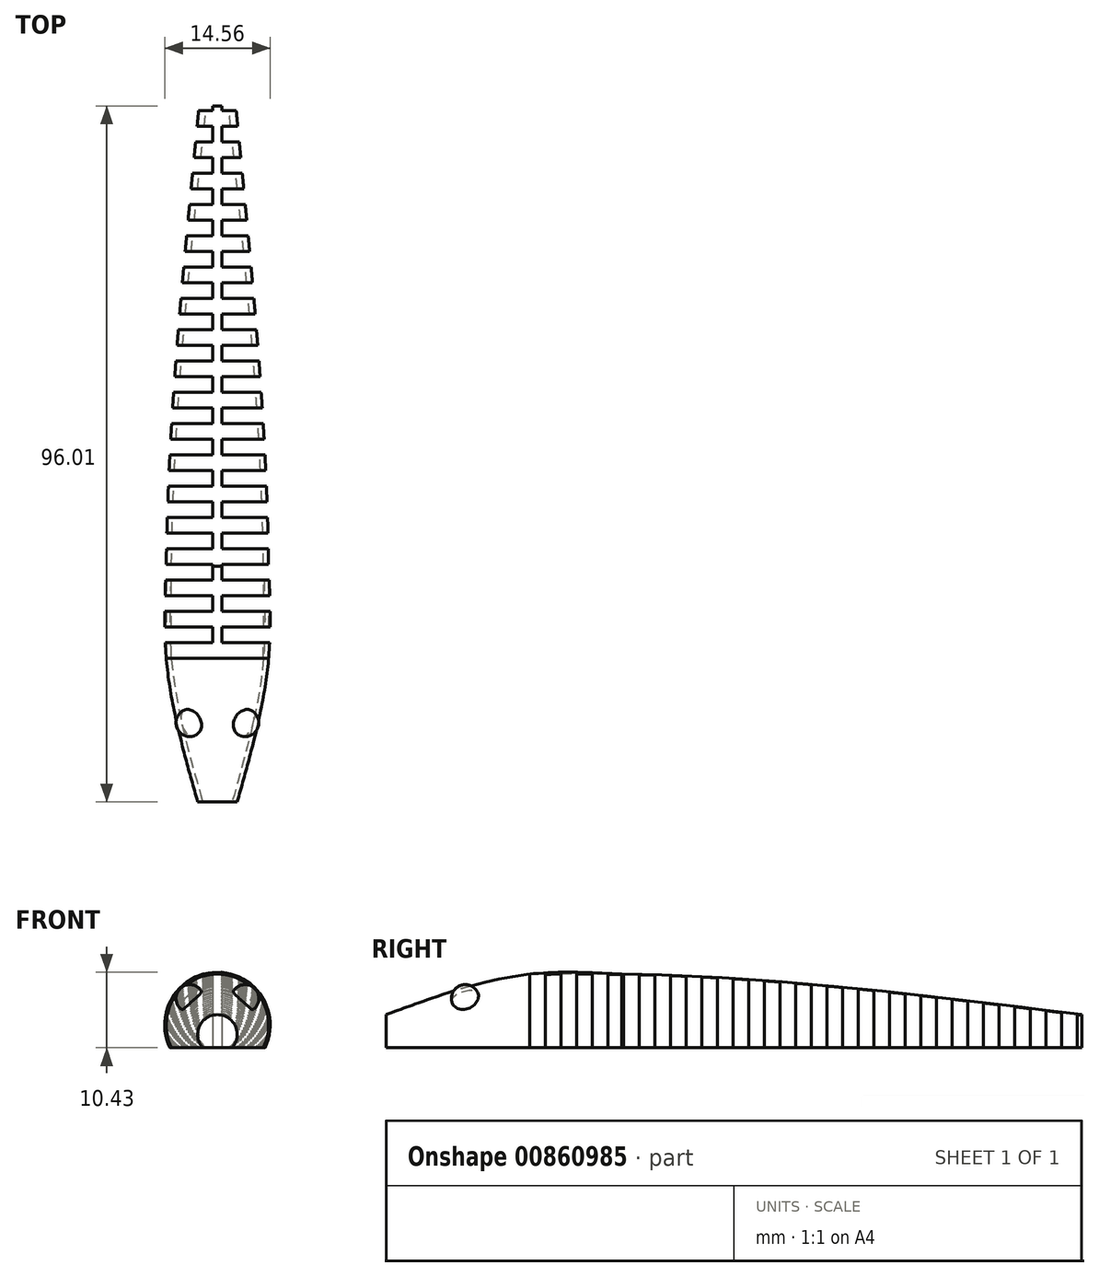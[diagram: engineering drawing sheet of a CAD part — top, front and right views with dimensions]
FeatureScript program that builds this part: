
annotation { "Feature Type Name" : "Feature", "Feature Type Description" : "" }
export const myFeature = defineFeature(function(context is Context, id is Id, definition is map)
    precondition{}
    {
        {
            var Q0;
            Q0=qCreatedBy(makeId("Front.planeOp"),FACE);
            var sketch = newSketch(context, id + "F0", { "sketchPlane" : qUnion([Q0])});
            skArc(sketch, "E0", {"start": v(6.35, 0) * mm, "mid": v(0, 10.16) * mm, "end": v(-6.35, 0) * mm});
            skPoint(sketch, "E0.first.point", {"position": v(-6.35, 0) * mm});
            skPoint(sketch, "E0.second.point", {"position": v(6.35, 0) * mm});
            skPoint(sketch, "E0.third.point", {"position": v(0, 10.16) * mm});
            skLineSegment(sketch, "E1", {"start": v(-6.35, 0) * mm, "end": v(6.35, 0) * mm});
            skSolve(sketch);
        }
        {
            var Q0;
            Q0=qCreatedBy(makeId("Front.planeOp"),FACE);
            cPlane(context, id + "F1", {"entities" : qUnion([Q0]), "cplaneType" : CPlaneType.OFFSET, "offset" : 12.7 * mm, "oppositeDirection" : true, "width" : 152.4 * mm, "height" : 152.4 * mm});
        }
        {
            var Q0;
            Q0=qCreatedBy(id+"F1.planeOp",FACE);
            var sketch = newSketch(context, id + "F2", { "sketchPlane" : qUnion([Q0])});
            skArc(sketch, "E2.0", {"start": v(6.35, 0) * mm, "mid": v(0, 10.16) * mm, "end": v(-6.35, 0) * mm});
            skLineSegment(sketch, "E2.1", {"start": v(-6.35, 0) * mm, "end": v(6.35, 0) * mm});
            skSolve(sketch);
        }
        {
            var Q0;
            Q0=qCreatedBy(id+"F1.planeOp",FACE);
            cPlane(context, id + "F3", {"entities" : qUnion([Q0]), "cplaneType" : CPlaneType.OFFSET, "offset" : 63.5 * mm, "oppositeDirection" : true, "width" : 152.4 * mm, "height" : 152.4 * mm});
        }
        {
            var Q0;
            Q0=qCreatedBy(id+"F3.planeOp",FACE);
            var sketch = newSketch(context, id + "F4", { "sketchPlane" : qUnion([Q0])});
            skPoint(sketch, "E3.0", {"position": v(0, 10.16) * mm});
            skPoint(sketch, "E4.0", {"position": v(6.35, 0) * mm});
            skPoint(sketch, "E5.0", {"position": v(-6.35, 0) * mm});
            skArc(sketch, "E6", {"start": v(1.52, 0) * mm, "mid": v(0, 4.57) * mm, "end": v(-1.52, 0) * mm});
            skPoint(sketch, "E6.first.point", {"position": v(1.52, 0) * mm});
            skPoint(sketch, "E6.second.point", {"position": v(-1.52, 0) * mm});
            skPoint(sketch, "E6.third.point", {"position": v(0, 4.57) * mm});
            skLineSegment(sketch, "E7", {"start": v(1.52, 0) * mm, "end": v(-1.52, 0) * mm});
            skSolve(sketch);
        }
        {
            var Q0;
            Q0=qCreatedBy(makeId("Front.planeOp"),FACE);
            cPlane(context, id + "F5", {"entities" : qUnion([Q0]), "cplaneType" : CPlaneType.OFFSET, "offset" : 19.8 * mm, "width" : 152.4 * mm, "height" : 152.4 * mm});
        }
        {
            var Q0;
            Q0=qCreatedBy(id+"F5.planeOp",FACE);
            var sketch = newSketch(context, id + "F6", { "sketchPlane" : qUnion([Q0])});
            skArc(sketch, "E8", {"start": v(2.03, 0) * mm, "mid": v(0, 4.57) * mm, "end": v(-2.03, 0) * mm});
            skPoint(sketch, "E8.first.point", {"position": v(-2.03, 0) * mm});
            skPoint(sketch, "E8.second.point", {"position": v(2.03, 0) * mm});
            skPoint(sketch, "E8.third.point", {"position": v(0, 4.57) * mm});
            skLineSegment(sketch, "E9", {"start": v(-2.03, 0) * mm, "end": v(2.03, 0) * mm});
            skSolve(sketch);
        }
        {
            var Q0;
            Q0=makeQuery(id+"F0.imprint","IMPRINT",FACE,{"disambiguationData":[TD([[makeQuery(id+"F0.imprint","IMPRINT",EDGE,{"derivedFrom":sQuery(id+"F0.wireOp",EDGE,"E0")}),1.0]])]});
            var Q1;
            Q1=makeQuery(id+"F2.imprint","IMPRINT",FACE,{"disambiguationData":[TD([[makeQuery(id+"F2.imprint","IMPRINT",EDGE,{"derivedFrom":sQuery(id+"F2.wireOp",EDGE,"E2.0")}),1.0]])]});
            var Q2;
            Q2=makeQuery(id+"F4.imprint","IMPRINT",FACE,{"disambiguationData":[TD([[makeQuery(id+"F4.imprint","IMPRINT",EDGE,{"derivedFrom":sQuery(id+"F4.wireOp",EDGE,"E6")}),1.0]])]});
            loft(context, id + "F7", {"sheetProfilesArray" : [{ "sheetProfileEntities" : qUnion([Q0]) }, { "sheetProfileEntities" : qUnion([Q1]) }, { "sheetProfileEntities" : qUnion([Q2]) }]});
        }
        {
            var Q0;
            Q0 = qSketchRegion(id + "F2", true);
            var Q1;
            Q1 = qSketchRegion(id + "F0", true);
            var Q2;
            Q2 = qSketchRegion(id + "F6", true);
            loft(context, id + "F8", {"sheetProfilesArray" : [{ "sheetProfileEntities" : qUnion([Q0]) }, { "sheetProfileEntities" : qUnion([Q1]) }, { "sheetProfileEntities" : qUnion([Q2]) }]});
        }
        {
            var Q0;
            Q0=qCreatedBy(makeId("Top.planeOp"),FACE);
            var sketch = newSketch(context, id + "F9", { "sketchPlane" : qUnion([Q0])});
            skLineSegment(sketch, "E10.bottom", {"start": v(-9.53, 2.16) * mm, "end": v(-0.64, 2.16) * mm});
            skLineSegment(sketch, "E10.top", {"start": v(-9.53, 4.32) * mm, "end": v(-0.64, 4.32) * mm});
            skLineSegment(sketch, "E10.left", {"start": v(-9.53, 2.16) * mm, "end": v(-9.53, 4.32) * mm});
            skLineSegment(sketch, "E10.right", {"start": v(-0.64, 2.16) * mm, "end": v(-0.64, 4.32) * mm});
            skLineSegment(sketch, "E11", {"start": v(0, -25.2) * mm, "end": v(0, 80.38) * mm, "construction": true});
            skLineSegment(sketch, "E12.0.1.0", {"start": v(-9.53, 6.48) * mm, "end": v(-9.53, 8.64) * mm});
            skLineSegment(sketch, "E12.0.1.1", {"start": v(-0.64, 6.48) * mm, "end": v(-0.64, 8.64) * mm});
            skLineSegment(sketch, "E12.0.1.2", {"start": v(-9.53, 8.64) * mm, "end": v(-0.64, 8.64) * mm});
            skLineSegment(sketch, "E12.0.1.3", {"start": v(-9.53, 6.48) * mm, "end": v(-0.64, 6.48) * mm});
            skLineSegment(sketch, "E12.0.2.0", {"start": v(-9.53, 10.8) * mm, "end": v(-9.53, 12.95) * mm});
            skLineSegment(sketch, "E12.0.2.1", {"start": v(-0.64, 10.8) * mm, "end": v(-0.64, 12.95) * mm});
            skLineSegment(sketch, "E12.0.2.2", {"start": v(-9.53, 12.95) * mm, "end": v(-0.64, 12.95) * mm});
            skLineSegment(sketch, "E12.0.2.3", {"start": v(-9.53, 10.8) * mm, "end": v(-0.64, 10.8) * mm});
            skLineSegment(sketch, "E12.0.3.0", {"start": v(-9.53, 15.11) * mm, "end": v(-9.53, 17.27) * mm});
            skLineSegment(sketch, "E12.0.3.1", {"start": v(-0.64, 15.11) * mm, "end": v(-0.64, 17.27) * mm});
            skLineSegment(sketch, "E12.0.3.2", {"start": v(-9.53, 17.27) * mm, "end": v(-0.64, 17.27) * mm});
            skLineSegment(sketch, "E12.0.3.3", {"start": v(-9.53, 15.11) * mm, "end": v(-0.64, 15.11) * mm});
            skLineSegment(sketch, "E12.0.4.0", {"start": v(-9.53, 19.43) * mm, "end": v(-9.53, 21.6) * mm});
            skLineSegment(sketch, "E12.0.4.1", {"start": v(-0.64, 19.43) * mm, "end": v(-0.64, 21.59) * mm});
            skLineSegment(sketch, "E12.0.4.2", {"start": v(-9.53, 21.6) * mm, "end": v(-0.64, 21.6) * mm});
            skLineSegment(sketch, "E12.0.4.3", {"start": v(-9.53, 19.43) * mm, "end": v(-0.64, 19.43) * mm});
            skLineSegment(sketch, "E12.0.5.0", {"start": v(-9.53, 23.75) * mm, "end": v(-9.53, 25.9) * mm});
            skLineSegment(sketch, "E12.0.5.1", {"start": v(-0.64, 23.75) * mm, "end": v(-0.64, 25.9) * mm});
            skLineSegment(sketch, "E12.0.5.2", {"start": v(-9.53, 25.9) * mm, "end": v(-0.64, 25.9) * mm});
            skLineSegment(sketch, "E12.0.5.3", {"start": v(-9.53, 23.75) * mm, "end": v(-0.64, 23.75) * mm});
            skLineSegment(sketch, "E12.0.6.0", {"start": v(-9.53, 28.07) * mm, "end": v(-9.53, 30.23) * mm});
            skLineSegment(sketch, "E12.0.6.1", {"start": v(-0.64, 28.07) * mm, "end": v(-0.64, 30.23) * mm});
            skLineSegment(sketch, "E12.0.6.2", {"start": v(-9.53, 30.23) * mm, "end": v(-0.64, 30.23) * mm});
            skLineSegment(sketch, "E12.0.6.3", {"start": v(-9.53, 28.07) * mm, "end": v(-0.64, 28.07) * mm});
            skLineSegment(sketch, "E12.0.7.0", {"start": v(-9.53, 32.39) * mm, "end": v(-9.53, 34.54) * mm});
            skLineSegment(sketch, "E12.0.7.1", {"start": v(-0.64, 32.39) * mm, "end": v(-0.64, 34.54) * mm});
            skLineSegment(sketch, "E12.0.7.2", {"start": v(-9.53, 34.54) * mm, "end": v(-0.64, 34.54) * mm});
            skLineSegment(sketch, "E12.0.7.3", {"start": v(-9.53, 32.39) * mm, "end": v(-0.64, 32.39) * mm});
            skLineSegment(sketch, "E12.0.8.0", {"start": v(-9.53, 36.7) * mm, "end": v(-9.53, 38.86) * mm});
            skLineSegment(sketch, "E12.0.8.1", {"start": v(-0.64, 36.7) * mm, "end": v(-0.64, 38.86) * mm});
            skLineSegment(sketch, "E12.0.8.2", {"start": v(-9.53, 38.86) * mm, "end": v(-0.64, 38.86) * mm});
            skLineSegment(sketch, "E12.0.8.3", {"start": v(-9.53, 36.7) * mm, "end": v(-0.64, 36.7) * mm});
            skLineSegment(sketch, "E12.0.9.0", {"start": v(-9.53, 41.02) * mm, "end": v(-9.53, 43.18) * mm});
            skLineSegment(sketch, "E12.0.9.1", {"start": v(-0.64, 41.02) * mm, "end": v(-0.64, 43.18) * mm});
            skLineSegment(sketch, "E12.0.9.2", {"start": v(-9.53, 43.18) * mm, "end": v(-0.64, 43.18) * mm});
            skLineSegment(sketch, "E12.0.9.3", {"start": v(-9.53, 41.02) * mm, "end": v(-0.64, 41.02) * mm});
            skLineSegment(sketch, "E12.0.10.0", {"start": v(-9.53, 45.34) * mm, "end": v(-9.53, 47.5) * mm});
            skLineSegment(sketch, "E12.0.10.1", {"start": v(-0.64, 45.34) * mm, "end": v(-0.64, 47.5) * mm});
            skLineSegment(sketch, "E12.0.10.2", {"start": v(-9.53, 47.5) * mm, "end": v(-0.64, 47.5) * mm});
            skLineSegment(sketch, "E12.0.10.3", {"start": v(-9.53, 45.34) * mm, "end": v(-0.64, 45.34) * mm});
            skLineSegment(sketch, "E12.0.11.0", {"start": v(-9.53, 49.66) * mm, "end": v(-9.53, 51.82) * mm});
            skLineSegment(sketch, "E12.0.11.1", {"start": v(-0.64, 49.66) * mm, "end": v(-0.64, 51.82) * mm});
            skLineSegment(sketch, "E12.0.11.2", {"start": v(-9.53, 51.82) * mm, "end": v(-0.64, 51.82) * mm});
            skLineSegment(sketch, "E12.0.11.3", {"start": v(-9.53, 49.66) * mm, "end": v(-0.64, 49.66) * mm});
            skLineSegment(sketch, "E12.0.12.0", {"start": v(-9.53, 53.98) * mm, "end": v(-9.53, 56.13) * mm});
            skLineSegment(sketch, "E12.0.12.1", {"start": v(-0.64, 53.98) * mm, "end": v(-0.64, 56.13) * mm});
            skLineSegment(sketch, "E12.0.12.2", {"start": v(-9.53, 56.13) * mm, "end": v(-0.64, 56.13) * mm});
            skLineSegment(sketch, "E12.0.12.3", {"start": v(-9.53, 53.98) * mm, "end": v(-0.64, 53.98) * mm});
            skLineSegment(sketch, "E12.0.13.0", {"start": v(-9.53, 58.3) * mm, "end": v(-9.53, 60.45) * mm});
            skLineSegment(sketch, "E12.0.13.1", {"start": v(-0.64, 58.3) * mm, "end": v(-0.64, 60.45) * mm});
            skLineSegment(sketch, "E12.0.13.2", {"start": v(-9.53, 60.45) * mm, "end": v(-0.64, 60.45) * mm});
            skLineSegment(sketch, "E12.0.13.3", {"start": v(-9.53, 58.3) * mm, "end": v(-0.64, 58.3) * mm});
            skLineSegment(sketch, "E12.0.14.0", {"start": v(-9.53, 62.61) * mm, "end": v(-9.53, 64.77) * mm});
            skLineSegment(sketch, "E12.0.14.1", {"start": v(-0.64, 62.61) * mm, "end": v(-0.64, 64.77) * mm});
            skLineSegment(sketch, "E12.0.14.2", {"start": v(-9.53, 64.77) * mm, "end": v(-0.64, 64.77) * mm});
            skLineSegment(sketch, "E12.0.14.3", {"start": v(-9.53, 62.61) * mm, "end": v(-0.64, 62.61) * mm});
            skLineSegment(sketch, "E12.0.15.0", {"start": v(-9.53, 66.93) * mm, "end": v(-9.53, 69.09) * mm});
            skLineSegment(sketch, "E12.0.15.1", {"start": v(-0.64, 66.93) * mm, "end": v(-0.64, 69.09) * mm});
            skLineSegment(sketch, "E12.0.15.2", {"start": v(-9.53, 69.09) * mm, "end": v(-0.64, 69.09) * mm});
            skLineSegment(sketch, "E12.0.15.3", {"start": v(-9.53, 66.93) * mm, "end": v(-0.64, 66.93) * mm});
            skLineSegment(sketch, "E12.0.16.0", {"start": v(-9.53, 71.25) * mm, "end": v(-9.53, 73.4) * mm});
            skLineSegment(sketch, "E12.0.16.1", {"start": v(-0.64, 71.25) * mm, "end": v(-0.64, 73.4) * mm});
            skLineSegment(sketch, "E12.0.16.2", {"start": v(-9.53, 73.4) * mm, "end": v(-0.64, 73.4) * mm});
            skLineSegment(sketch, "E12.0.16.3", {"start": v(-9.53, 71.25) * mm, "end": v(-0.64, 71.25) * mm});
            skLineSegment(sketch, "E12.0.17.0", {"start": v(-9.53, 75.57) * mm, "end": v(-9.53, 77.72) * mm});
            skLineSegment(sketch, "E12.0.17.1", {"start": v(-0.64, 75.57) * mm, "end": v(-0.64, 77.72) * mm});
            skLineSegment(sketch, "E12.0.17.2", {"start": v(-9.53, 77.72) * mm, "end": v(-0.64, 77.72) * mm});
            skLineSegment(sketch, "E12.0.17.3", {"start": v(-9.53, 75.57) * mm, "end": v(-0.64, 75.57) * mm});
            skLineSegment(sketch, "E12.direction1", {"start": v(-9.52, 2.16) * mm, "end": v(15.88, 2.16) * mm, "construction": true});
            skLineSegment(sketch, "E12.direction2", {"start": v(-9.53, 2.16) * mm, "end": v(-9.53, 6.48) * mm, "construction": true});
            skLineSegment(sketch, "E13.MirrorCS", {"start": v(9.53, 66.93) * mm, "end": v(9.53, 69.09) * mm});
            skLineSegment(sketch, "E14.MirrorCS", {"start": v(9.53, 41.02) * mm, "end": v(9.53, 43.18) * mm});
            skLineSegment(sketch, "E15.MirrorCS", {"start": v(0.64, 36.7) * mm, "end": v(0.64, 38.86) * mm});
            skLineSegment(sketch, "E16.MirrorCS", {"start": v(0.64, 75.57) * mm, "end": v(0.64, 77.72) * mm});
            skLineSegment(sketch, "E17.MirrorCS", {"start": v(9.53, 6.48) * mm, "end": v(9.53, 8.64) * mm});
            skLineSegment(sketch, "E18.MirrorCS", {"start": v(0.64, 62.61) * mm, "end": v(0.64, 64.77) * mm});
            skLineSegment(sketch, "E19.MirrorCS", {"start": v(0.64, 2.16) * mm, "end": v(0.64, 4.32) * mm});
            skLineSegment(sketch, "E20.MirrorCS", {"start": v(9.53, 36.7) * mm, "end": v(9.53, 38.86) * mm});
            skLineSegment(sketch, "E21.MirrorCS", {"start": v(9.53, 32.39) * mm, "end": v(9.53, 34.54) * mm});
            skLineSegment(sketch, "E22.MirrorCS", {"start": v(0.64, 41.02) * mm, "end": v(0.64, 43.18) * mm});
            skLineSegment(sketch, "E23.MirrorCS", {"start": v(9.53, 62.61) * mm, "end": v(9.53, 64.77) * mm});
            skLineSegment(sketch, "E24.MirrorCS", {"start": v(0.64, 32.39) * mm, "end": v(0.64, 34.54) * mm});
            skLineSegment(sketch, "E25.MirrorCS", {"start": v(9.53, 2.16) * mm, "end": v(9.53, 4.32) * mm});
            skLineSegment(sketch, "E26.MirrorCS", {"start": v(0.64, 10.8) * mm, "end": v(0.64, 12.95) * mm});
            skLineSegment(sketch, "E27.MirrorCS", {"start": v(9.53, 10.8) * mm, "end": v(9.53, 12.95) * mm});
            skLineSegment(sketch, "E28.MirrorCS", {"start": v(0.64, 66.93) * mm, "end": v(0.64, 69.09) * mm});
            skLineSegment(sketch, "E29.MirrorCS", {"start": v(0.64, 6.48) * mm, "end": v(0.64, 8.64) * mm});
            skLineSegment(sketch, "E30.MirrorCS", {"start": v(0.64, 71.25) * mm, "end": v(0.64, 73.4) * mm});
            skLineSegment(sketch, "E31.MirrorCS", {"start": v(9.53, 23.75) * mm, "end": v(9.53, 25.9) * mm});
            skLineSegment(sketch, "E32.MirrorCS", {"start": v(9.53, 19.43) * mm, "end": v(9.53, 21.6) * mm});
            skLineSegment(sketch, "E33.MirrorCS", {"start": v(9.53, 25.9) * mm, "end": v(0.64, 25.9) * mm});
            skLineSegment(sketch, "E34.MirrorCS", {"start": v(9.53, 41.02) * mm, "end": v(0.64, 41.02) * mm});
            skLineSegment(sketch, "E35.MirrorCS", {"start": v(9.53, 45.34) * mm, "end": v(0.64, 45.34) * mm});
            skLineSegment(sketch, "E36.MirrorCS", {"start": v(0.64, 45.34) * mm, "end": v(0.64, 47.5) * mm});
            skLineSegment(sketch, "E37.MirrorCS", {"start": v(9.53, 69.09) * mm, "end": v(0.64, 69.09) * mm});
            skLineSegment(sketch, "E38.MirrorCS", {"start": v(9.53, 58.3) * mm, "end": v(0.64, 58.3) * mm});
            skLineSegment(sketch, "E39.MirrorCS", {"start": v(9.53, 77.72) * mm, "end": v(0.64, 77.72) * mm});
            skLineSegment(sketch, "E40.MirrorCS", {"start": v(9.53, 21.6) * mm, "end": v(0.64, 21.6) * mm});
            skLineSegment(sketch, "E41.MirrorCS", {"start": v(9.53, 71.25) * mm, "end": v(9.53, 73.4) * mm});
            skLineSegment(sketch, "E42.MirrorCS", {"start": v(9.53, 66.93) * mm, "end": v(0.64, 66.93) * mm});
            skLineSegment(sketch, "E43.MirrorCS", {"start": v(9.53, 15.11) * mm, "end": v(0.64, 15.11) * mm});
            skLineSegment(sketch, "E44.MirrorCS", {"start": v(9.53, 62.61) * mm, "end": v(0.64, 62.61) * mm});
            skLineSegment(sketch, "E45.MirrorCS", {"start": v(0.64, 53.98) * mm, "end": v(0.64, 56.13) * mm});
            skLineSegment(sketch, "E46.MirrorCS", {"start": v(9.53, 75.57) * mm, "end": v(0.64, 75.57) * mm});
            skLineSegment(sketch, "E47.MirrorCS", {"start": v(0.64, 23.75) * mm, "end": v(0.64, 25.9) * mm});
            skLineSegment(sketch, "E48.MirrorCS", {"start": v(9.53, 15.11) * mm, "end": v(9.53, 17.27) * mm});
            skLineSegment(sketch, "E49.MirrorCS", {"start": v(9.53, 73.4) * mm, "end": v(0.64, 73.4) * mm});
            skLineSegment(sketch, "E50.MirrorCS", {"start": v(0.64, 28.07) * mm, "end": v(0.64, 30.23) * mm});
            skLineSegment(sketch, "E51.MirrorCS", {"start": v(9.53, 71.25) * mm, "end": v(0.64, 71.25) * mm});
            skLineSegment(sketch, "E52.MirrorCS", {"start": v(9.53, 49.66) * mm, "end": v(0.64, 49.66) * mm});
            skLineSegment(sketch, "E53.MirrorCS", {"start": v(9.53, 58.3) * mm, "end": v(9.53, 60.45) * mm});
            skLineSegment(sketch, "E54.MirrorCS", {"start": v(9.53, 51.82) * mm, "end": v(0.64, 51.82) * mm});
            skLineSegment(sketch, "E55.MirrorCS", {"start": v(9.53, 49.66) * mm, "end": v(9.53, 51.82) * mm});
            skLineSegment(sketch, "E56.MirrorCS", {"start": v(9.53, 12.95) * mm, "end": v(0.64, 12.95) * mm});
            skLineSegment(sketch, "E57.MirrorCS", {"start": v(9.53, 64.77) * mm, "end": v(0.64, 64.77) * mm});
            skLineSegment(sketch, "E58.MirrorCS", {"start": v(9.53, 28.07) * mm, "end": v(9.53, 30.23) * mm});
            skLineSegment(sketch, "E59.MirrorCS", {"start": v(9.53, 19.43) * mm, "end": v(0.64, 19.43) * mm});
            skLineSegment(sketch, "E60.MirrorCS", {"start": v(9.53, 45.34) * mm, "end": v(9.53, 47.5) * mm});
            skLineSegment(sketch, "E61.MirrorCS", {"start": v(9.53, 56.13) * mm, "end": v(0.64, 56.13) * mm});
            skLineSegment(sketch, "E62.MirrorCS", {"start": v(9.53, 28.07) * mm, "end": v(0.64, 28.07) * mm});
            skLineSegment(sketch, "E63.MirrorCS", {"start": v(9.53, 38.86) * mm, "end": v(0.64, 38.86) * mm});
            skLineSegment(sketch, "E64.MirrorCS", {"start": v(9.53, 47.5) * mm, "end": v(0.64, 47.5) * mm});
            skLineSegment(sketch, "E65.MirrorCS", {"start": v(0.64, 58.3) * mm, "end": v(0.64, 60.45) * mm});
            skLineSegment(sketch, "E66.MirrorCS", {"start": v(9.53, 8.64) * mm, "end": v(0.64, 8.64) * mm});
            skLineSegment(sketch, "E67.MirrorCS", {"start": v(9.53, 30.23) * mm, "end": v(0.64, 30.23) * mm});
            skLineSegment(sketch, "E68.MirrorCS", {"start": v(0.64, 49.66) * mm, "end": v(0.64, 51.82) * mm});
            skLineSegment(sketch, "E69.MirrorCS", {"start": v(9.53, 6.48) * mm, "end": v(0.64, 6.48) * mm});
            skLineSegment(sketch, "E70.MirrorCS", {"start": v(0.64, 19.43) * mm, "end": v(0.64, 21.59) * mm});
            skLineSegment(sketch, "E71.MirrorCS", {"start": v(9.53, 4.32) * mm, "end": v(0.64, 4.32) * mm});
            skLineSegment(sketch, "E72.MirrorCS", {"start": v(9.53, 23.75) * mm, "end": v(0.64, 23.75) * mm});
            skLineSegment(sketch, "E73.MirrorCS", {"start": v(9.53, 2.16) * mm, "end": v(9.53, 6.48) * mm, "construction": true});
            skLineSegment(sketch, "E74.MirrorCS", {"start": v(0.64, 15.11) * mm, "end": v(0.64, 17.27) * mm});
            skLineSegment(sketch, "E75.MirrorCS", {"start": v(9.53, 53.98) * mm, "end": v(0.64, 53.98) * mm});
            skLineSegment(sketch, "E76.MirrorCS", {"start": v(9.53, 75.57) * mm, "end": v(9.53, 77.72) * mm});
            skLineSegment(sketch, "E77.MirrorCS", {"start": v(9.53, 43.18) * mm, "end": v(0.64, 43.18) * mm});
            skLineSegment(sketch, "E78.MirrorCS", {"start": v(9.53, 2.16) * mm, "end": v(0.64, 2.16) * mm});
            skLineSegment(sketch, "E79.MirrorCS", {"start": v(9.53, 17.27) * mm, "end": v(0.64, 17.27) * mm});
            skLineSegment(sketch, "E80.MirrorCS", {"start": v(9.53, 10.8) * mm, "end": v(0.64, 10.8) * mm});
            skLineSegment(sketch, "E81.MirrorCS", {"start": v(9.53, 60.45) * mm, "end": v(0.64, 60.45) * mm});
            skLineSegment(sketch, "E82.MirrorCS", {"start": v(9.53, 34.54) * mm, "end": v(0.64, 34.54) * mm});
            skLineSegment(sketch, "E83.MirrorCS", {"start": v(9.53, 36.7) * mm, "end": v(0.64, 36.7) * mm});
            skLineSegment(sketch, "E84.MirrorCS", {"start": v(9.53, 32.39) * mm, "end": v(0.64, 32.39) * mm});
            skLineSegment(sketch, "E85.MirrorCS", {"start": v(9.53, 53.98) * mm, "end": v(9.53, 56.13) * mm});
            skSolve(sketch);
        }
        {
            var Q0;
            Q0 = qSketchRegion(id + "F9", true);
            extrude(context, id + "F10", {"entities" : qUnion([Q0]), "operationType" : NewBodyOperationType.REMOVE, "endBound" : BoundingType.THROUGH_ALL, "depth" : 25.4 * mm, "offsetDistance" : 25.4 * mm});
        }
        {
            var Q0;
            Q0=qCreatedBy(makeId("Right.planeOp"),FACE);
            cPlane(context, id + "F11", {"entities" : qUnion([Q0]), "cplaneType" : CPlaneType.OFFSET, "offset" : 3.8 * mm, "width" : 152.4 * mm, "height" : 152.4 * mm});
        }
        {
            var Q0;
            Q0=qCreatedBy(id+"F11.planeOp",FACE);
            var sketch = newSketch(context, id + "F12", { "sketchPlane" : qUnion([Q0])});
            skFitSpline(sketch, "E86", {"points": [v(12.7, 9.04) * mm, v(10.8, 9.17) * mm, v(7.93, 9.34) * mm, v(4.1, 9.36) * mm, v(1.24, 9.22) * mm, v(-1.57, 8.85) * mm, v(-4.34, 8.26) * mm, v(-7.08, 7.47) * mm, v(-8.89, 6.83) * mm, v(-9.78, 6.48) * mm, v(-10.5, 6.18) * mm, v(-11.59, 5.72) * mm, v(-12.99, 5.01) * mm, v(-13.67, 4.62) * mm, v(-14, 4.4) * mm, v(-14.15, 4.31) * mm, v(-14.45, 4.11) * mm, v(-14.88, 3.79) * mm, v(-15.29, 3.43) * mm, v(-15.53, 3.16) * mm, v(-15.63, 3.02) * mm, v(-15.75, 2.86) * mm, v(-15.9, 2.6) * mm, v(-15.96, 2.21) * mm, v(-15.94, 2.02) * mm, v(-15.92, 1.93) * mm, v(-15.87, 1.73) * mm, v(-15.65, 1.37) * mm, v(-15.34, 1.09) * mm, v(-15.18, 0.96) * mm, v(-14.91, 0.76) * mm, v(-14.33, 0.41) * mm, v(-13.72, 0.13) * mm, v(-13.4, 0) * mm]});
            skFitSpline(sketch, "E87", {"points": [v(12.7, 9.04) * mm, v(10.8, 9.17) * mm, v(7.93, 9.34) * mm, v(4.1, 9.36) * mm, v(1.24, 9.22) * mm, v(-1.57, 8.85) * mm, v(-4.34, 8.26) * mm, v(-7.08, 7.47) * mm, v(-8.89, 6.83) * mm, v(-9.78, 6.48) * mm, v(-10.5, 6.18) * mm, v(-11.59, 5.72) * mm, v(-12.99, 5.01) * mm, v(-13.67, 4.62) * mm, v(-14, 4.4) * mm, v(-14.15, 4.31) * mm, v(-14.45, 4.11) * mm, v(-14.88, 3.79) * mm, v(-15.29, 3.43) * mm, v(-15.53, 3.16) * mm, v(-15.63, 3.02) * mm, v(-15.75, 2.86) * mm, v(-15.9, 2.6) * mm, v(-15.96, 2.21) * mm, v(-15.94, 2.02) * mm, v(-15.92, 1.93) * mm, v(-15.87, 1.73) * mm, v(-15.65, 1.37) * mm, v(-15.34, 1.09) * mm, v(-15.18, 0.96) * mm, v(-14.91, 0.76) * mm, v(-14.33, 0.41) * mm, v(-13.72, 0.13) * mm, v(-13.4, 0) * mm]});
            skFitSpline(sketch, "E88", {"points": [v(12.7, 9.04) * mm, v(10.8, 9.17) * mm, v(7.93, 9.34) * mm, v(4.1, 9.36) * mm, v(1.24, 9.22) * mm, v(-1.57, 8.85) * mm, v(-4.34, 8.26) * mm, v(-7.08, 7.47) * mm, v(-8.89, 6.83) * mm, v(-9.78, 6.48) * mm, v(-10.5, 6.18) * mm, v(-11.59, 5.72) * mm, v(-12.99, 5.01) * mm, v(-13.67, 4.62) * mm, v(-14, 4.4) * mm, v(-14.15, 4.31) * mm, v(-14.45, 4.11) * mm, v(-14.88, 3.79) * mm, v(-15.29, 3.43) * mm, v(-15.53, 3.16) * mm, v(-15.63, 3.02) * mm, v(-15.75, 2.86) * mm, v(-15.9, 2.6) * mm, v(-15.96, 2.21) * mm, v(-15.94, 2.02) * mm, v(-15.92, 1.93) * mm, v(-15.87, 1.73) * mm, v(-15.65, 1.37) * mm, v(-15.34, 1.09) * mm, v(-15.18, 0.96) * mm, v(-14.91, 0.76) * mm, v(-14.33, 0.41) * mm, v(-13.72, 0.13) * mm, v(-13.4, 0) * mm]});
            skPoint(sketch, "E89", {"position": v(-8.9, 6.82) * mm});
            skArc(sketch, "E90", {"start": v(-6.99, 6.82) * mm, "mid": v(-8.9, 8.72) * mm, "end": v(-10.8, 6.82) * mm});
            skLineSegment(sketch, "E91", {"start": v(-8.9, 6.82) * mm, "end": v(-6.99, 6.82) * mm});
            skLineSegment(sketch, "E92", {"start": v(-8.9, 6.82) * mm, "end": v(-10.8, 6.82) * mm});
            skFitSpline(sketch, "E93.trimOffspring", {"points": [v(12.7, 9.04) * mm, v(10.8, 9.17) * mm, v(7.93, 9.34) * mm, v(4.1, 9.36) * mm, v(1.24, 9.22) * mm, v(-1.57, 8.85) * mm, v(-4.34, 8.26) * mm, v(-7.08, 7.47) * mm, v(-8.89, 6.83) * mm, v(-9.78, 6.48) * mm, v(-10.5, 6.18) * mm, v(-11.59, 5.72) * mm, v(-12.99, 5.01) * mm, v(-13.67, 4.62) * mm, v(-14, 4.4) * mm, v(-14.15, 4.31) * mm, v(-14.45, 4.11) * mm, v(-14.88, 3.79) * mm, v(-15.29, 3.43) * mm, v(-15.53, 3.16) * mm, v(-15.63, 3.02) * mm, v(-15.75, 2.86) * mm, v(-15.9, 2.6) * mm, v(-15.96, 2.21) * mm, v(-15.94, 2.02) * mm, v(-15.92, 1.93) * mm, v(-15.87, 1.73) * mm, v(-15.65, 1.37) * mm, v(-15.34, 1.09) * mm, v(-15.18, 0.96) * mm, v(-14.91, 0.76) * mm, v(-14.33, 0.41) * mm, v(-13.72, 0.13) * mm, v(-13.4, 0) * mm]});
            skSolve(sketch);
        }
        {
            var Q0;
            Q0 = qSketchRegion(id + "F12", true);
            var Q1;
            Q1=sQuery(id+"F12.wireOp",EDGE,"E92");
            revolve(context, id + "F13", {"surfaceOperationType" : NewSurfaceOperationType.NEW, "entities" : qUnion([Q0]), "axis" : qUnion([Q1]), "revolveType" : RevolveType.FULL});
        }
        {
            var Q0;
            Q0=makeQuery(id+"F13.opRevolve","SWEPT_BODY",BODY,{"disambiguationData":[OSD([sQuery(id+"F12.wireOp",EDGE,"E90"),sQuery(id+"F12.wireOp",EDGE,"E91"),sQuery(id+"F12.wireOp",EDGE,"E92")])]});
            var Q1;
            Q1=qCreatedBy(makeId("Right.planeOp"),FACE);
            mirror(context, id + "F14", {"operationType" : NewBodyOperationType.ADD, "entities" : qUnion([Q0]), "mirrorPlane" : qUnion([Q1])});
        }
    });
